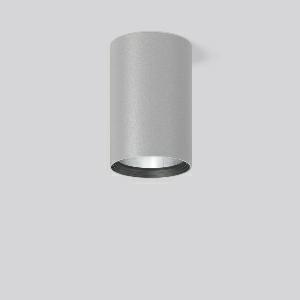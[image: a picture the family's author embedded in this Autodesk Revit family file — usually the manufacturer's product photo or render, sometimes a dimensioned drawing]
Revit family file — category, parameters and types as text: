
# Revit family: heledon_maxi_a_931237_004_a51e
name_source: partatom
category: Lighting Fixtures
units: mm (PartAtom-declared; Revit-internal decimal feet)

## family parameters
Cut with Voids When Loaded = No
Host = Face
Light Source = No
Part Type = Normal
Room Calculation Point = No
Round Connector Dimension = Use Diameter
Shared = No

## types (1)
- HELEDON maxi A (1 x LED Modul 920 meat+, 2200 lm, 2000)
    Apparent Load = 33 VA
    Approval mark = CE
    CIE Flux Codes = 100 100 100 100 100
    Color Rendering = 90
    Color Temperature = 2000
    Default Elevation = 1800 mm
    Description = Series: HELEDON maxi
Cylindrical surface-mounted downlight. Housing: die-cast aluminium, powder-coated. Internal ceiling frame polycarbonate with bayonet mounting. Black plastic ring and recessed LED to prevent glare from the side. Optical assembly with reflector made of MIRO-Silver with 98% total light reflection for outstanding efficiency - can be changed without tools. Special LED for illumination of meat included. Suitable for Ceiling mounting. Easy installation with a separate ceiling frame with bayonet mounting and plug connection. Driver integrated. Connected via plug-in connector. High quality converter without flickering and stroboscopic effect. The following accessories can be mounted without use of tools: interchangeable lenses, decorative glasses, honeycomb louvre, clear and frosted diffusers, white interchangeable plastic ring. 
Colour: silver
Diameter: 123 mm
Height: 183 mm
Lamp: LED
Socket: without socket
Colour temperature: meat +
System power: 33 W
Rated luminous flux: 2200 lm
Luminous efficiency: 67 lm/W
Control gear: Regulated power supply
Protection class: I
Type of protection: IP 20
    Height = 183 mm
    Lamp = 1 x LED Modul 920 meat+
    Lamp Light Flux = 2200 lm
    Lamp count = 1
    Length = 123 mm
    Lifetime = 50000 h
    Luminous efficacy = 67 lm/W
    Manufacturer = RZB
    ModVariant = No
    Model = 931237.004
    Mounting Place = Ceiling
    Mounting Type = Surface mounted
    Number of Poles = 1
    OnlyDefault = Yes
    Power Factor = 1
    Product Name = HELEDON maxi A
    Product group = Surface mounted downlights
    ProductGroupID = 302
    Protection Class = Protection class I
    Protection Degree = IP 20
    RLX_Detail_Level = 1
    RLX_Emergency_Light_Flux = 0 lm
    RLX_Emergency_Type = 0
    RLX_Emergency_Type_DB = No
    RlxData = <blob elided: 98537 chars, md5=d814be3c>
    Socket = socket
    Standby Power = 0 W
    System Light Flux = 2200 lm
    System Power = 33 W
    Type Comments = Product without accessories
    Type Image = 931192.004.jpg
    URL = http://relux.com
    VarID = ---
    Voltage = 230 V
    Voltage Range = 220-240 V
    Weight = 0.00 kg
    Width = 0 mm  [stored 0 ft]

note: [stored X ft] marks values corroborated as IEEE doubles in the binary element streams (Revit-internal decimal feet)

## geometry (parser evidence)
native form markers: Blend x4, Sweep x10
no freeform markers — native parametric forms only
